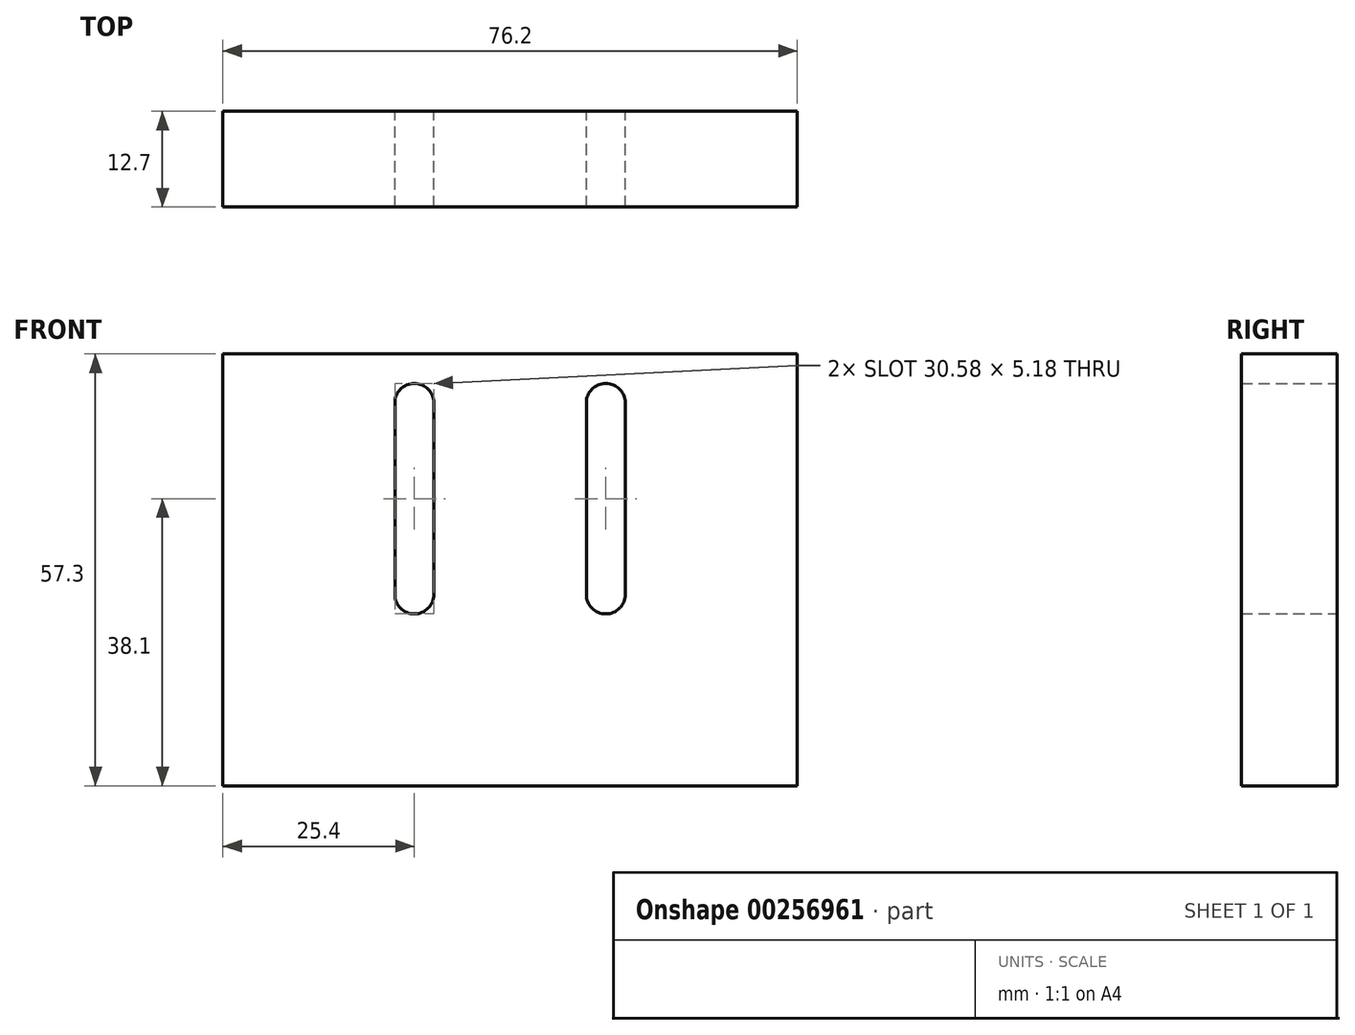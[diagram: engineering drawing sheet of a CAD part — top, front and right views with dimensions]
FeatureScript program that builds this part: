
annotation { "Feature Type Name" : "Feature", "Feature Type Description" : "" }
export const myFeature = defineFeature(function(context is Context, id is Id, definition is map)
    precondition{}
    {
        {
            var Q0;
            Q0=qCreatedBy(makeId("Front.planeOp"),FACE);
            var sketch = newSketch(context, id + "F0", { "sketchPlane" : qUnion([Q0])});
            skLineSegment(sketch, "E0.bottom", {"start": v(-38.1, 57.3) * mm, "end": v(38.1, 57.3) * mm});
            skLineSegment(sketch, "E0.top", {"start": v(-38.1, 0) * mm, "end": v(38.1, 0) * mm});
            skLineSegment(sketch, "E0.left", {"start": v(-38.1, 57.3) * mm, "end": v(-38.1, 0) * mm});
            skLineSegment(sketch, "E0.right", {"start": v(38.1, 57.3) * mm, "end": v(38.1, 0) * mm});
            skCircle(sketch, "E1", {"center": v(-12.7, 50.8) * mm, "radius": 2.6 * mm});
            skCircle(sketch, "E2", {"center": v(-12.7, 25.4) * mm, "radius": 2.6 * mm});
            skCircle(sketch, "E3", {"center": v(-12.7, 50.8) * mm, "radius": 3.96 * mm});
            skCircle(sketch, "E4", {"center": v(-12.7, 25.4) * mm, "radius": 3.96 * mm});
            skCircle(sketch, "E5", {"center": v(-12.7, 50.8) * mm, "radius": 6.38 * mm});
            skCircle(sketch, "E6", {"center": v(-12.7, 25.4) * mm, "radius": 6.35 * mm});
            skLineSegment(sketch, "E7", {"start": v(0, 0) * mm, "end": v(0, 57.3) * mm});
            skLineSegment(sketch, "E8.bottom", {"start": v(-10.1, 50.8) * mm, "end": v(-15.3, 50.8) * mm});
            skLineSegment(sketch, "E8.top", {"start": v(-10.1, 25.4) * mm, "end": v(-15.3, 25.4) * mm});
            skLineSegment(sketch, "E8.left", {"start": v(-10.1, 50.8) * mm, "end": v(-10.1, 25.4) * mm});
            skLineSegment(sketch, "E8.right", {"start": v(-15.3, 50.8) * mm, "end": v(-15.3, 25.4) * mm});
            skLineSegment(sketch, "E9.MirrorCS", {"start": v(10.1, 50.8) * mm, "end": v(10.1, 25.4) * mm});
            skLineSegment(sketch, "E10.MirrorCS", {"start": v(15.3, 50.8) * mm, "end": v(15.3, 25.4) * mm});
            skCircle(sketch, "E11.MirrorC", {"center": v(12.7, 50.8) * mm, "radius": 2.6 * mm});
            skCircle(sketch, "E12.MirrorC", {"center": v(12.7, 25.4) * mm, "radius": 2.6 * mm});
            skSolve(sketch);
        }
        {
            var Q0;
            {var subQ5=sQuery(id+"F0.wireOp",EDGE,"E0.left");Q0=makeQuery(id+"F0.imprint","IMPRINT",FACE,{"disambiguationData":[TD([[makeQuery(id+"F0.imprint","IMPRINT",EDGE,{"derivedFrom":subQ5}),1.0]])]});}
            var Q1;
            {var subQ0=sQuery(id+"F0.wireOp",EDGE,"E8.left");var subQ1=sQuery(id+"F0.wireOp",EDGE,"E3");var subQ2=makeQuery(id+"F0.imprint","INTERSECT",VERTEX,{"derivedFrom":[subQ1,subQ0]});Q1=makeQuery(id+"F0.imprint","IMPRINT",FACE,{"disambiguationData":[TD([[makeQuery(id+"F0.imprint","IMPRINT",EDGE,{"disambiguationData":[TD([[subQ2,-1.0]])],"derivedFrom":subQ1}),-1.0]])]});}
            var Q2;
            {var subQ0=sQuery(id+"F0.wireOp",EDGE,"E8.left");var subQ6=sQuery(id+"F0.wireOp",EDGE,"E3");var subQ7=makeQuery(id+"F0.imprint","INTERSECT",VERTEX,{"derivedFrom":[subQ6,subQ0]});Q2=makeQuery(id+"F0.imprint","IMPRINT",FACE,{"disambiguationData":[TD([[makeQuery(id+"F0.imprint","IMPRINT",EDGE,{"disambiguationData":[TD([[subQ7,-1.0]])],"derivedFrom":subQ6}),1.0]])]});}
            var Q3;
            {var subQ0=sQuery(id+"F0.wireOp",EDGE,"E8.left");var subQ6=sQuery(id+"F0.wireOp",EDGE,"E4");var subQ7=makeQuery(id+"F0.imprint","INTERSECT",VERTEX,{"derivedFrom":[subQ6,subQ0]});Q3=makeQuery(id+"F0.imprint","IMPRINT",FACE,{"disambiguationData":[TD([[makeQuery(id+"F0.imprint","IMPRINT",EDGE,{"disambiguationData":[TD([[subQ7,1.0]])],"derivedFrom":subQ6}),1.0]])]});}
            var Q4;
            {var subQ0=sQuery(id+"F0.wireOp",EDGE,"E8.left");var subQ1=sQuery(id+"F0.wireOp",EDGE,"E4");var subQ2=makeQuery(id+"F0.imprint","INTERSECT",VERTEX,{"derivedFrom":[subQ1,subQ0]});Q4=makeQuery(id+"F0.imprint","IMPRINT",FACE,{"disambiguationData":[TD([[makeQuery(id+"F0.imprint","IMPRINT",EDGE,{"disambiguationData":[TD([[subQ2,1.0]])],"derivedFrom":subQ1}),-1.0]])]});}
            var Q5;
            {var subQ0=sQuery(id+"F0.wireOp",EDGE,"E0.right");Q5=makeQuery(id+"F0.imprint","IMPRINT",FACE,{"disambiguationData":[TD([[makeQuery(id+"F0.imprint","IMPRINT",EDGE,{"derivedFrom":subQ0}),-1.0]])]});}
            extrude(context, id + "F1", {"entities" : qUnion([Q0, Q1, Q2, Q3, Q4, Q5]), "depth" : 12.7 * mm});
        }
    });
